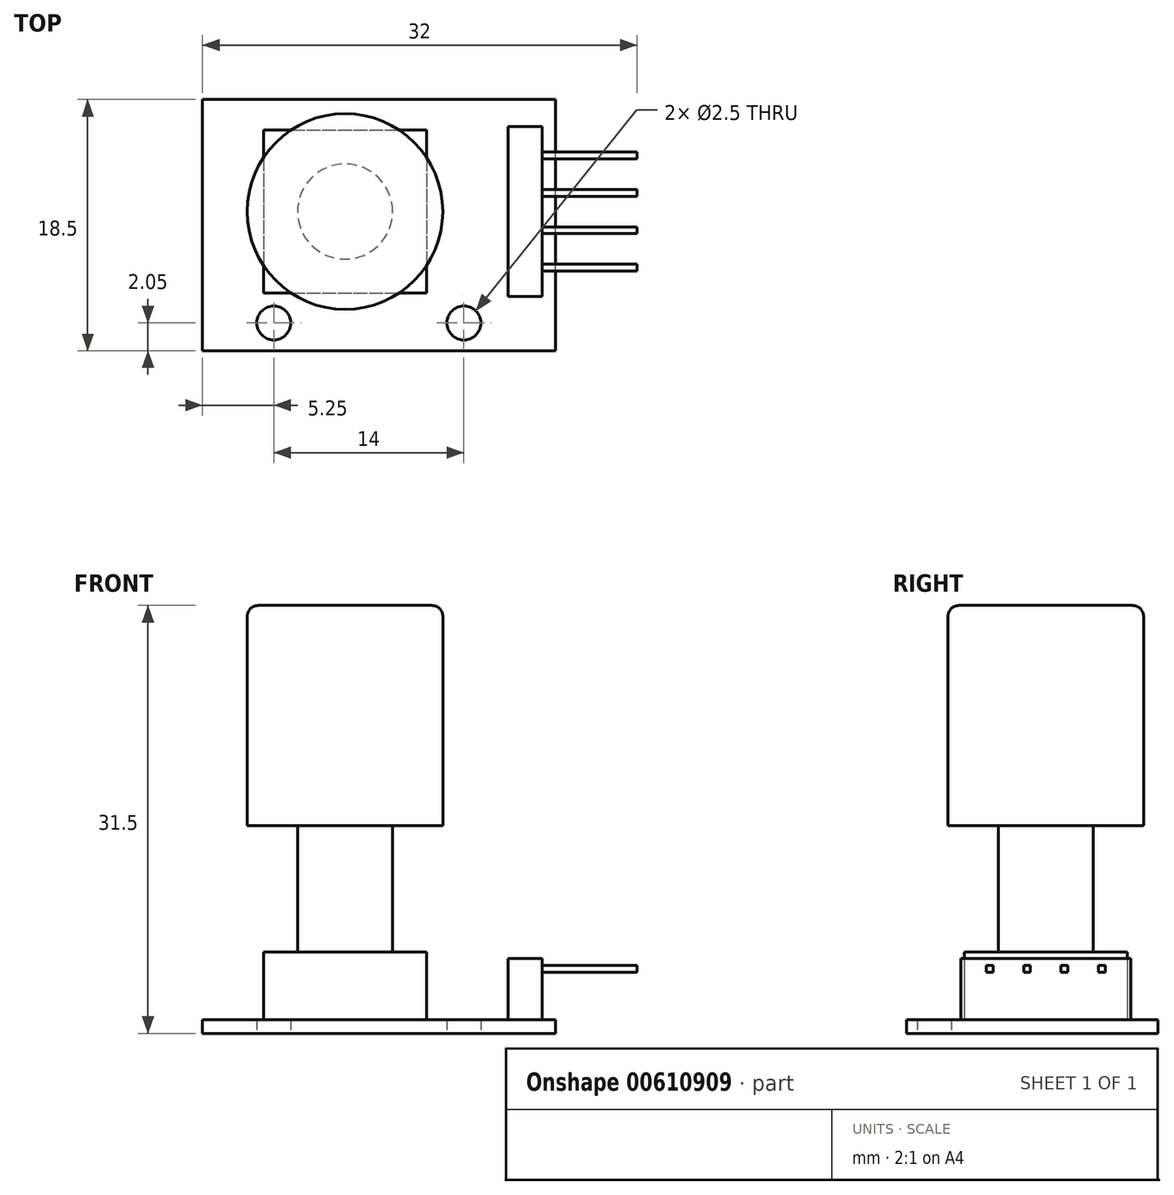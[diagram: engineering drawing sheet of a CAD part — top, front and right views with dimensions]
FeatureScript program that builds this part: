
annotation { "Feature Type Name" : "Feature", "Feature Type Description" : "" }
export const myFeature = defineFeature(function(context is Context, id is Id, definition is map)
    precondition{}
    {
        {
            var Q0;
            Q0=qCreatedBy(makeId("Top.planeOp"),FACE);
            var sketch = newSketch(context, id + "F0", { "sketchPlane" : qUnion([Q0])});
            skLineSegment(sketch, "E0.bottom", {"start": v(13, -9.25) * mm, "end": v(-13, -9.25) * mm});
            skLineSegment(sketch, "E0.top", {"start": v(13, 9.25) * mm, "end": v(-13, 9.25) * mm});
            skLineSegment(sketch, "E0.left", {"start": v(13, -9.25) * mm, "end": v(13, 9.25) * mm});
            skLineSegment(sketch, "E0.right", {"start": v(-13, -9.25) * mm, "end": v(-13, 9.25) * mm});
            skPoint(sketch, "E0.middle", {"position": v(0, 0) * mm});
            skCircle(sketch, "E1", {"center": v(-7.75, -7.2) * mm, "radius": 1.25 * mm});
            skCircle(sketch, "E2", {"center": v(6.25, -7.2) * mm, "radius": 1.25 * mm});
            skSolve(sketch);
        }
        {
            var Q0;
            Q0 = qSketchRegion(id + "F0", true);
            extrude(context, id + "F1", {"entities" : qUnion([Q0]), "depth" : 1 * mm, "offsetDistance" : 25 * mm});
        }
        {
            var Q0;
            Q0=makeQuery(id+"F1.opExtrude","CAP_FACE",FACE,{"disambiguationData":[OSD([sQuery(id+"F0.wireOp",EDGE,"E0.bottom"),sQuery(id+"F0.wireOp",EDGE,"E0.top"),sQuery(id+"F0.wireOp",EDGE,"E0.left"),sQuery(id+"F0.wireOp",EDGE,"E0.right"),sQuery(id+"F0.wireOp",EDGE,"E1"),sQuery(id+"F0.wireOp",EDGE,"E2")])],"isStart":false});
            var sketch = newSketch(context, id + "F2", { "sketchPlane" : qUnion([Q0])});
            skLineSegment(sketch, "E3.bottom", {"start": v(-8.5, 7) * mm, "end": v(3.5, 7) * mm});
            skLineSegment(sketch, "E3.top", {"start": v(-8.5, -5) * mm, "end": v(3.5, -5) * mm});
            skLineSegment(sketch, "E3.left", {"start": v(-8.5, 7) * mm, "end": v(-8.5, -5) * mm});
            skLineSegment(sketch, "E3.right", {"start": v(3.5, 7) * mm, "end": v(3.5, -5) * mm});
            skSolve(sketch);
        }
        {
            var Q0;
            Q0 = qSketchRegion(id + "F2", true);
            extrude(context, id + "F3", {"entities" : qUnion([Q0]), "operationType" : NewBodyOperationType.ADD, "depth" : 5 * mm, "offsetDistance" : 25 * mm});
        }
        {
            var Q0;
            Q0=makeQuery(id+"F3.opExtrude","CAP_FACE",FACE,{"disambiguationData":[OSD([sQuery(id+"F2.wireOp",EDGE,"E3.bottom"),sQuery(id+"F2.wireOp",EDGE,"E3.top"),sQuery(id+"F2.wireOp",EDGE,"E3.left"),sQuery(id+"F2.wireOp",EDGE,"E3.right")])],"isStart":false});
            var sketch = newSketch(context, id + "F4", { "sketchPlane" : qUnion([Q0])});
            skCircle(sketch, "E4", {"center": v(-2.5, 1) * mm, "radius": 3.5 * mm});
            skSolve(sketch);
        }
        {
            var Q0;
            Q0=makeQuery(id+"F4.imprint","IMPRINT",FACE,{"disambiguationData":[TD([[makeQuery(id+"F4.imprint","IMPRINT",EDGE,{"derivedFrom":sQuery(id+"F4.wireOp",EDGE,"E4")}),1.0]])]});
            extrude(context, id + "F5", {"entities" : qUnion([Q0]), "operationType" : NewBodyOperationType.ADD, "depth" : 9.3 * mm, "offsetDistance" : 25 * mm});
        }
        {
            var Q0;
            Q0=makeQuery(id+"F5.opExtrude","CAP_FACE",FACE,{"disambiguationData":[OSD([sQuery(id+"F4.wireOp",EDGE,"E4")])],"isStart":false});
            var sketch = newSketch(context, id + "F6", { "sketchPlane" : qUnion([Q0])});
            skCircle(sketch, "E5", {"center": v(-2.5, 1) * mm, "radius": 7.2 * mm});
            skSolve(sketch);
        }
        {
            var Q0;
            Q0 = qSketchRegion(id + "F6", true);
            extrude(context, id + "F7", {"entities" : qUnion([Q0]), "operationType" : NewBodyOperationType.ADD, "depth" : 16.2 * mm, "offsetDistance" : 25 * mm});
        }
        {
            var Q0;
            Q0=makeQuery(id+"F7.opExtrude","CAP_EDGE",EDGE,{"disambiguationData":[OSD([sQuery(id+"F6.wireOp",EDGE,"E5")])],"isStart":false});
            fillet(context, id + "F8", {"entities" : qUnion([Q0]), "radius" : 0.8 * mm, "tangentPropagation" : true, "allowEdgeOverflow" : false});
        }
        {
            var Q0;
            Q0=makeQuery(id+"F1.opExtrude","CAP_FACE",FACE,{"disambiguationData":[OSD([sQuery(id+"F0.wireOp",EDGE,"E0.bottom"),sQuery(id+"F0.wireOp",EDGE,"E0.top"),sQuery(id+"F0.wireOp",EDGE,"E0.left"),sQuery(id+"F0.wireOp",EDGE,"E0.right"),sQuery(id+"F0.wireOp",EDGE,"E1"),sQuery(id+"F0.wireOp",EDGE,"E2")])],"isStart":false});
            var sketch = newSketch(context, id + "F9", { "sketchPlane" : qUnion([Q0])});
            skLineSegment(sketch, "E6.bottom", {"start": v(9.5, 7.25) * mm, "end": v(12, 7.25) * mm});
            skLineSegment(sketch, "E6.top", {"start": v(9.5, -5.25) * mm, "end": v(12, -5.25) * mm});
            skLineSegment(sketch, "E6.left", {"start": v(9.5, 7.25) * mm, "end": v(9.5, -5.25) * mm});
            skLineSegment(sketch, "E6.right", {"start": v(12, 7.25) * mm, "end": v(12, -5.25) * mm});
            skSolve(sketch);
        }
        {
            var Q0;
            Q0=makeQuery(id+"F9.imprint","IMPRINT",FACE,{"disambiguationData":[TD([[makeQuery(id+"F9.imprint","IMPRINT",EDGE,{"derivedFrom":sQuery(id+"F9.wireOp",EDGE,"E6.bottom")}),-1.0]])]});
            extrude(context, id + "F10", {"entities" : qUnion([Q0]), "operationType" : NewBodyOperationType.ADD, "depth" : 4.5 * mm, "offsetDistance" : 25 * mm});
        }
        {
            var Q0;
            Q0=makeQuery(id+"F10.opExtrude","SWEPT_FACE",FACE,{"disambiguationData":[OSD([sQuery(id+"F9.wireOp",EDGE,"E6.right")])]});
            var sketch = newSketch(context, id + "F11", { "sketchPlane" : qUnion([Q0])});
            skLineSegment(sketch, "E7.bottom", {"start": v(-2.88, 4.5) * mm, "end": v(-3.38, 4.5) * mm});
            skLineSegment(sketch, "E7.top", {"start": v(-2.87, 5) * mm, "end": v(-3.38, 5) * mm});
            skLineSegment(sketch, "E7.left", {"start": v(-2.88, 4.5) * mm, "end": v(-2.88, 5) * mm});
            skLineSegment(sketch, "E7.right", {"start": v(-3.38, 4.5) * mm, "end": v(-3.38, 5) * mm});
            skPoint(sketch, "E7.middle", {"position": v(-3.12, 4.76) * mm});
            skPoint(sketch, "E8.1.0.0", {"position": v(-0.37, 4.76) * mm});
            skLineSegment(sketch, "E8.1.0.1", {"start": v(-0.13, 4.5) * mm, "end": v(-0.63, 4.5) * mm});
            skLineSegment(sketch, "E8.1.0.2", {"start": v(-0.12, 5) * mm, "end": v(-0.63, 5) * mm});
            skLineSegment(sketch, "E8.1.0.3", {"start": v(-0.13, 4.5) * mm, "end": v(-0.13, 5) * mm});
            skLineSegment(sketch, "E8.1.0.4", {"start": v(-0.63, 4.5) * mm, "end": v(-0.63, 5) * mm});
            skPoint(sketch, "E8.2.0.0", {"position": v(2.38, 4.76) * mm});
            skLineSegment(sketch, "E8.2.0.1", {"start": v(2.62, 4.5) * mm, "end": v(2.13, 4.5) * mm});
            skLineSegment(sketch, "E8.2.0.2", {"start": v(2.63, 5) * mm, "end": v(2.13, 5) * mm});
            skLineSegment(sketch, "E8.2.0.3", {"start": v(2.62, 4.5) * mm, "end": v(2.62, 5) * mm});
            skLineSegment(sketch, "E8.2.0.4", {"start": v(2.12, 4.5) * mm, "end": v(2.12, 5) * mm});
            skPoint(sketch, "E8.3.0.0", {"position": v(5.13, 4.76) * mm});
            skLineSegment(sketch, "E8.3.0.1", {"start": v(5.38, 4.5) * mm, "end": v(4.88, 4.5) * mm});
            skLineSegment(sketch, "E8.3.0.2", {"start": v(5.38, 5) * mm, "end": v(4.88, 5) * mm});
            skLineSegment(sketch, "E8.3.0.3", {"start": v(5.38, 4.5) * mm, "end": v(5.38, 5) * mm});
            skLineSegment(sketch, "E8.3.0.4", {"start": v(4.88, 4.5) * mm, "end": v(4.88, 5) * mm});
            skLineSegment(sketch, "E8.direction1", {"start": v(-3.38, 4.5) * mm, "end": v(-0.63, 4.5) * mm, "construction": true});
            skLineSegment(sketch, "E9", {"start": v(-3.38, 5) * mm, "end": v(-5.25, 5) * mm, "construction": true});
            skLineSegment(sketch, "E10", {"start": v(5.38, 5) * mm, "end": v(7.25, 5) * mm, "construction": true});
            skSolve(sketch);
        }
        {
            var Q0;
            Q0 = qSketchRegion(id + "F11", true);
            extrude(context, id + "F12", {"entities" : qUnion([Q0]), "operationType" : NewBodyOperationType.ADD, "depth" : 7 * mm, "offsetDistance" : 25 * mm});
        }
    });
